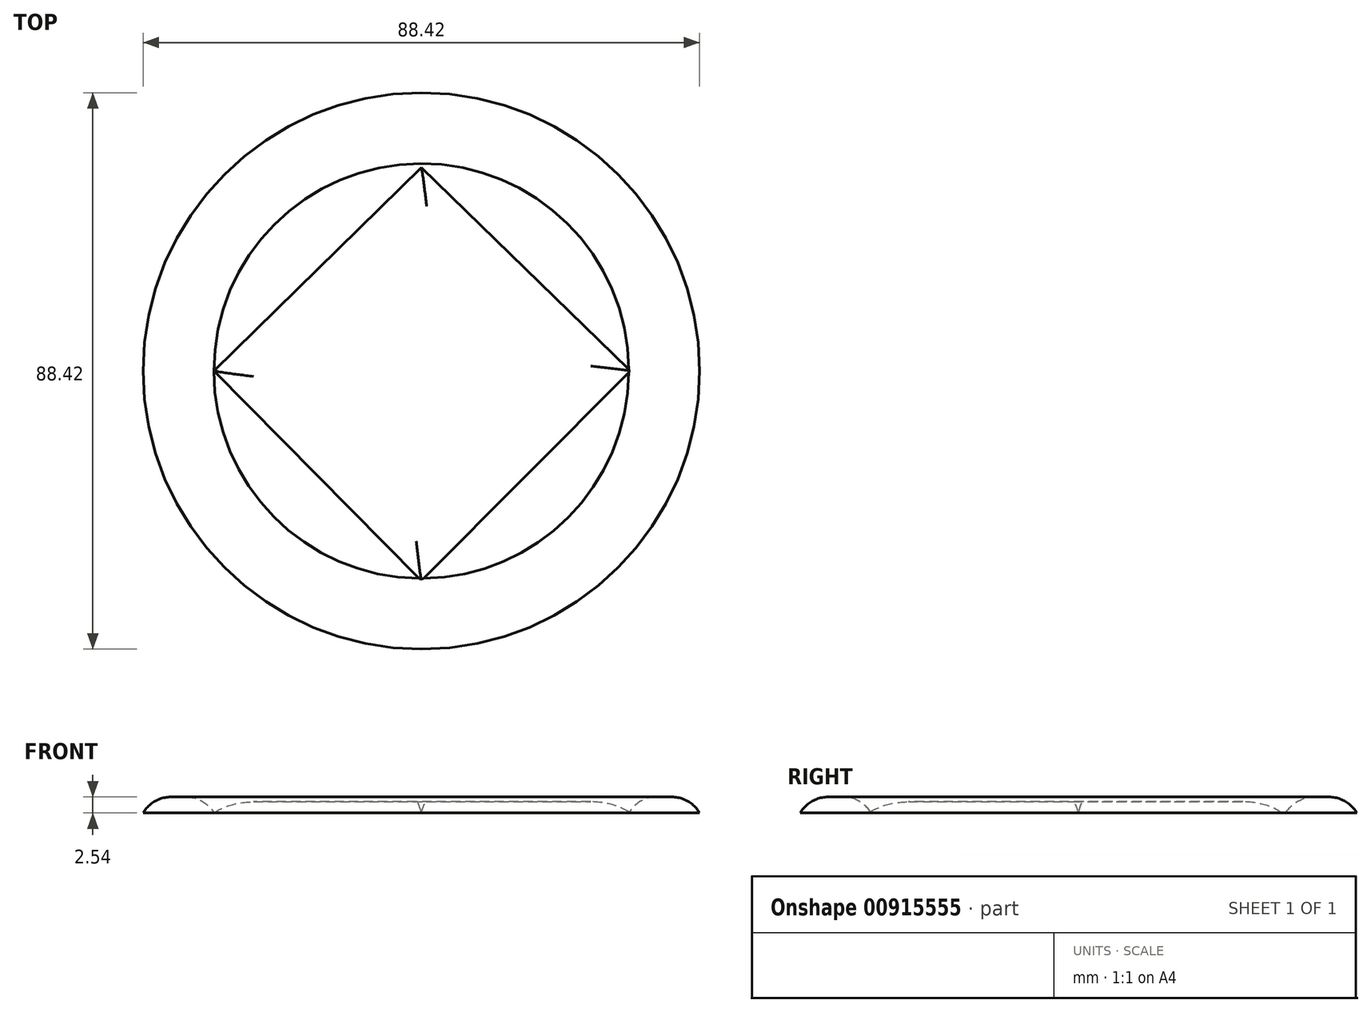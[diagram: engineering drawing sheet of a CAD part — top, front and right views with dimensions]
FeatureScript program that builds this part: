
annotation { "Feature Type Name" : "Feature", "Feature Type Description" : "" }
export const myFeature = defineFeature(function(context is Context, id is Id, definition is map)
    precondition{}
    {
        {
            var Q0;
            Q0=qCreatedBy(makeId("Top.planeOp"),FACE);
            var sketch = newSketch(context, id + "F0", { "sketchPlane" : qUnion([Q0])});
            skCircle(sketch, "E0", {"center": v(0, 0) * mm, "radius": 44.21 * mm});
            skCircle(sketch, "E1", {"center": v(0, 0) * mm, "radius": 32.97 * mm});
            skSolve(sketch);
        }
        {
            var Q0;
            Q0=makeQuery(id+"F0.imprint","IMPRINT",FACE,{"disambiguationData":[TD([[makeQuery(id+"F0.imprint","IMPRINT",EDGE,{"derivedFrom":sQuery(id+"F0.wireOp",EDGE,"E0")}),1.0]])]});
            extrude(context, id + "F1", {"entities" : qUnion([Q0]), "depth" : 2.54 * mm, "offsetDistance" : 25.4 * mm});
        }
        {
            var Q0;
            Q0=makeQuery(id+"F1.opExtrude","CAP_EDGE",EDGE,{"disambiguationData":[OSD([sQuery(id+"F0.wireOp",EDGE,"E0")])],"isStart":false});
            var Q1;
            Q1=makeQuery(id+"F1.opExtrude","CAP_EDGE",EDGE,{"disambiguationData":[OSD([sQuery(id+"F0.wireOp",EDGE,"E1")])],"isStart":false});
            fillet(context, id + "F2", {"entities" : qUnion([Q0, Q1]), "radius" : 5.08 * mm, "tangentPropagation" : true, "allowEdgeOverflow" : false});
        }
        {
            var Q0;
            Q0=qCreatedBy(makeId("Top.planeOp"),FACE);
            var sketch = newSketch(context, id + "F3", { "sketchPlane" : qUnion([Q0])});
            skLineSegment(sketch, "E2", {"start": v(33.22, 0) * mm, "end": v(0, 32.35) * mm});
            skLineSegment(sketch, "E3", {"start": v(0, 32.35) * mm, "end": v(-32.97, 0) * mm});
            skLineSegment(sketch, "E4", {"start": v(0, -33.35) * mm, "end": v(33.22, 0) * mm});
            skLineSegment(sketch, "E5", {"start": v(-32.97, 0) * mm, "end": v(0, -33.35) * mm});
            skSolve(sketch);
        }
        {
            var Q0;
            Q0=makeQuery(id+"F3.imprint","IMPRINT",FACE,{"disambiguationData":[TD([[makeQuery(id+"F3.imprint","IMPRINT",EDGE,{"derivedFrom":sQuery(id+"F3.wireOp",EDGE,"E2")}),1.0]])]});
            extrude(context, id + "F4", {"entities" : qUnion([Q0]), "operationType" : NewBodyOperationType.ADD, "depth" : 1.78 * mm, "offsetDistance" : 25.4 * mm});
        }
        {
            var Q0;
            Q0=makeQuery(id+"F4.opExtrude","CAP_EDGE",EDGE,{"disambiguationData":[OSD([sQuery(id+"F3.wireOp",EDGE,"E5")])],"isStart":false});
            var Q1;
            Q1=makeQuery(id+"F4.opExtrude","CAP_EDGE",EDGE,{"disambiguationData":[OSD([sQuery(id+"F3.wireOp",EDGE,"E2")])],"isStart":false});
            fillet(context, id + "F5", {"entities" : qUnion([Q0, Q1]), "radius" : 5.08 * mm, "tangentPropagation" : true, "allowEdgeOverflow" : false});
        }
        {
            var Q0;
            Q0=makeQuery(id+"F4.opExtrude","CAP_EDGE",EDGE,{"disambiguationData":[OSD([sQuery(id+"F3.wireOp",EDGE,"E3")])],"isStart":false});
            var Q1;
            Q1=makeQuery(id+"F4.opExtrude","CAP_EDGE",EDGE,{"disambiguationData":[OSD([sQuery(id+"F3.wireOp",EDGE,"E4")])],"isStart":false});
            fillet(context, id + "F6", {"entities" : qUnion([Q0, Q1]), "radius" : 7.97 * mm, "tangentPropagation" : true, "allowEdgeOverflow" : false});
        }
    });
